# Revit family: Faucet-Kitchen-KOHLER-Contra-K-26448T-1
name_source: partatom
category: Plumbing Fixtures
units: mm (PartAtom-declared; Revit-internal decimal feet)

## family parameters
Cut with Voids When Loaded = No
Host = Face
OmniClass Number = 23.31.11.00
OmniClass Title = Faucets
Part Type = Normal
Room Calculation Point = No
Round Connector Dimension = Use Diameter
Shared = No

## types (4) — shared parameters
ADA Compliant = No
Assembly Code = D2010
CW Connection = Yes
Cold Water Inlet = Cold Water Inlet
Date Modified = 02/03/2024
Default Elevation = 36"
Description = Pull-Down Kitchen Faucet
Drain Included = No
Flow Rate = 2 GPM
HW Connection = Yes
Handle Clearance = 4 3/8"
Height = 16 11/16"
Hot Water Inlet = Hot Water Inlet
Length = 8 7/8"
Manufacturer = Kohler Co.
Master Format 2014 = 22 41 39
Master Format 2014 Name = Residential Faucets, Supplies, and Trim
Material = Premium Metal Construction
Pressure = 60.00 psi
Product Documentation Link = https://files.kohler.com.cn
Product Name = Contra
Spout Reach = 8 7/8"
URL = http://www.kohler.com.cn
Vent Connection = No
Waste Connection = No
Waste Water Outlet = Waste Water Outlet
WaterSense Certified = No
Width = 2 1/4"

## per-type parameters (varying)
| type | Finish | Model | Product Page URL | Type |
| CP-Polished Chrome | Kohler-Metal-CP-Polished_Chrome | K-26448T-4-CP | https://www.kohler.com.cn | 1 |
| VS-Vibrant Stainless | Kohler-Metal-VS-Vibrant_Stainless | K-26448T-4-VS | https://www.kohler.com.cn | 2 |
| BRD-Brushed Rose Gold | KOHLER-Metal-BRD-Brushed_Rose_Gold | K-26448T-4-BRD |  | 3 |
| BRT-Brushed Titanium | KOHLER-Metal-BRT-Brushed_Titanium | K-26448T-4-BRT |  | 4 |

## geometry (parser evidence)
native form markers: Sweep x5
no freeform markers — native parametric forms only
